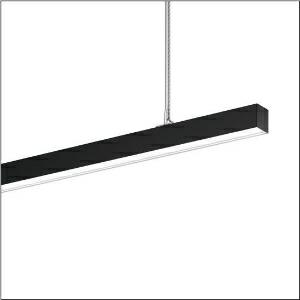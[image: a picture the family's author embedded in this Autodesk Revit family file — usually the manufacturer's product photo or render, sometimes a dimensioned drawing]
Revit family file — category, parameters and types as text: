
# Revit family: silica_21_51mx33db49bb
name_source: partatom
category: Lighting Fixtures
units: mm (PartAtom-declared; Revit-internal decimal feet)

## family parameters
Cut with Voids When Loaded = No
Host = Face
Light Source = No
Part Type = Normal
Room Calculation Point = No
Round Connector Dimension = Use Diameter
Shared = No

## types (1)
- --- (1 x LED, 7390 lm, 48.3 W, 4000K)
    Apparent Load = 48 VA
    CIE Flux Codes = 78 96 99 55 100
    Color Rendering = 80
    Color Temperature = 4000K
    Default Elevation = 1800 mm
    Description = Silica 21, office luminaire, primary optical cover: prismatic diffuser, of PMMA, CAT 2 (L<= 3000cd/m²), light emission: direct/indirect distribution, primary light characteristic: symmetric, installation type: suspended mounting, LED, rated luminous flux: 7.390lm, luminous efficacy: 153lm/W, light colour: 840, colour temperature: 4000K, control gear: DALI 2, with terminal, 3+2-pole, max. 2.5mm², mains connection: 220..240V, AC, 50/60Hz, rated input power: 48.3W, luminaire housing, of aluminium, matt jet black (RAL 9005), length: 1.504mm, width: 53mm, height: 53mm, protection rating (complete): IP20, insulation class (complete): insulation class I (protective earthing), certification: CE, permissible operating ambient temperature: 0..+35°C, standard: EN 50419, packaging unit: 1 piece
    Height = 53 mm
    Lamp = 1 x LED
    Lamp Light Flux = 7390 lm
    Lamp Power = 48.3 W
    Lamp count = 1
    Length = 1504 mm
    Luminous efficacy = 153 lm/W
    Manufacturer = Siteco
    ModVariant = No
    Model = 51MX33DB49BB
    Mounting Place = Ceiling
    Mounting Type = Pendant
    Number of Poles = 1
    OnlyDefault = Yes
    Power Factor = 1
    Product Name = Silica 21
    Product group = office luminaire | ceiling pendant
    ProductGroupID = 903
    Protection Class = Protection class I
    Protection Degree = IP 20
    RLX_Detail_Level = 1
    RLX_Emergency_Light_Flux = 0 lm
    RLX_Emergency_Type = 0
    RLX_Emergency_Type_DB = No
    RlxData = <blob elided: 26261 chars, md5=765354c0>
    Socket = socket
    Standby Power = 0 W
    System Light Flux = 7390 lm
    System Power = 48 W
    Type Comments = factory setting: luminous flux: 100 % | dim-lin: 254 | 323 mA
    Type Image = l_1335856.jpg
    URL = http://relux.com
    VarID = @adj_118587
    Voltage = 0 V
    Weight = 0.00 kg
    Width = 53 mm

## geometry (parser evidence)
native form markers: Blend x4, Sweep x14
no freeform markers — native parametric forms only
